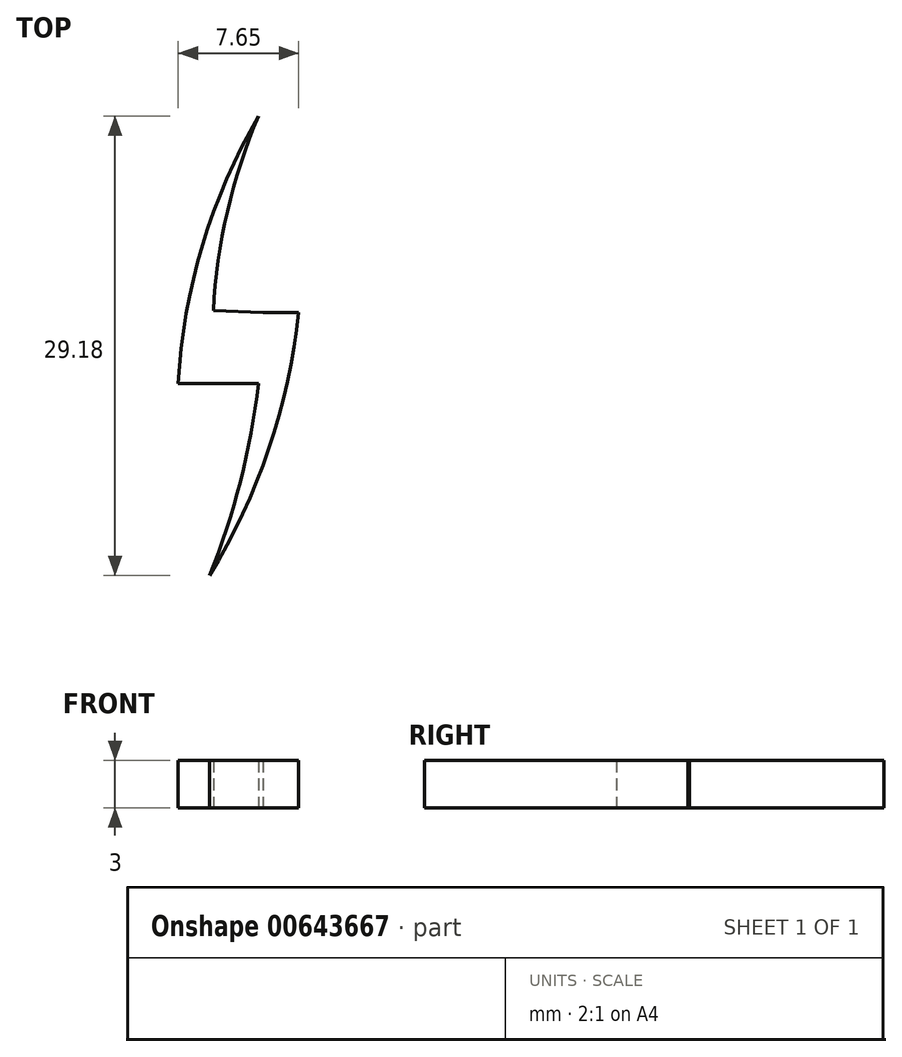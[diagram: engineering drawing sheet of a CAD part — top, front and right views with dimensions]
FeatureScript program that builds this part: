
annotation { "Feature Type Name" : "Feature", "Feature Type Description" : "" }
export const myFeature = defineFeature(function(context is Context, id is Id, definition is map)
    precondition{}
    {
        {
            var Q0;
            Q0=qCreatedBy(makeId("Top.planeOp"),FACE);
            var sketch = newSketch(context, id + "F0", { "sketchPlane" : qUnion([Q0])});
            skArc(sketch, "E0", {"start": v(-25.92, 41.5) * mm, "mid": v(-29.48, 33.3) * mm, "end": v(-31.02, 24.5) * mm});
            skArc(sketch, "E1", {"start": v(-25.92, 41.5) * mm, "mid": v(-28.35, 33.17) * mm, "end": v(-28.73, 24.5) * mm});
            skArc(sketch, "E2", {"start": v(-29.04, 12.32) * mm, "mid": v(-25.27, 20.36) * mm, "end": v(-23.37, 29.04) * mm});
            skArc(sketch, "E3", {"start": v(-29.04, 12.32) * mm, "mid": v(-26.56, 20.52) * mm, "end": v(-25.62, 29.04) * mm});
            skLineSegment(sketch, "E4", {"start": v(-25.62, 29.04) * mm, "end": v(-23.37, 29.04) * mm});
            skLineSegment(sketch, "E5", {"start": v(-31.02, 24.5) * mm, "end": v(-28.73, 24.5) * mm});
            skLineSegment(sketch, "E6", {"start": v(-28.79, 29.14) * mm, "end": v(-25.62, 29.04) * mm});
            skLineSegment(sketch, "E7", {"start": v(-25.92, 24.5) * mm, "end": v(-28.73, 24.5) * mm});
            skSolve(sketch);
        }
        {
            var Q0;
            Q0 = qSketchRegion(id + "F0", true);
            extrude(context, id + "F1", {"entities" : qUnion([Q0]), "depth" : 3 * mm, "offsetDistance" : 25 * mm});
        }
    });
